# Revit family: Тройник переходной ВР
name_source: partatom
category: Соединительные детали трубопроводов
revit_build: Autodesk Revit 2017 (Build: 20160225_1515(x64)
units: mm (PartAtom-declared; Revit-internal decimal feet)

## family parameters
Всегда вертикально = Да
На основе рабочей плоскости = Нет
Общий = Нет
При загрузке вырезать с полостями = Нет
Размер круглого соединителя = Использовать радиус
Тип детали = Тройник

## types (1)
- Тройник равнопроходной ВР
    ADSK_Единица измерения = шт
    ADSK_Завод-изготовитель = ООО САНЕКСТ.ПРО
    ADSK_Масса = 0
    ADSK_Материал наименование = DZR латунь
    ADSK_Расход жидкости = 0.0 л/с
    URL = http://sanext.ru
    Изготовитель = ООО САНЕКСТ.ПРО
    Материал фитинга = DZR латунь
    Описание = Тройник равнопроходной ВР
    Разработчик = ООО ПРОРУБИМ
    Разработчик (телефон) = +7(495)649-85-43
    Разработчик модели (URL) = http://prorubim.com
    Таблица_артикул = Тройник переходной ВР артикул
    Таблица_наименование = Тройник переходной ВР
